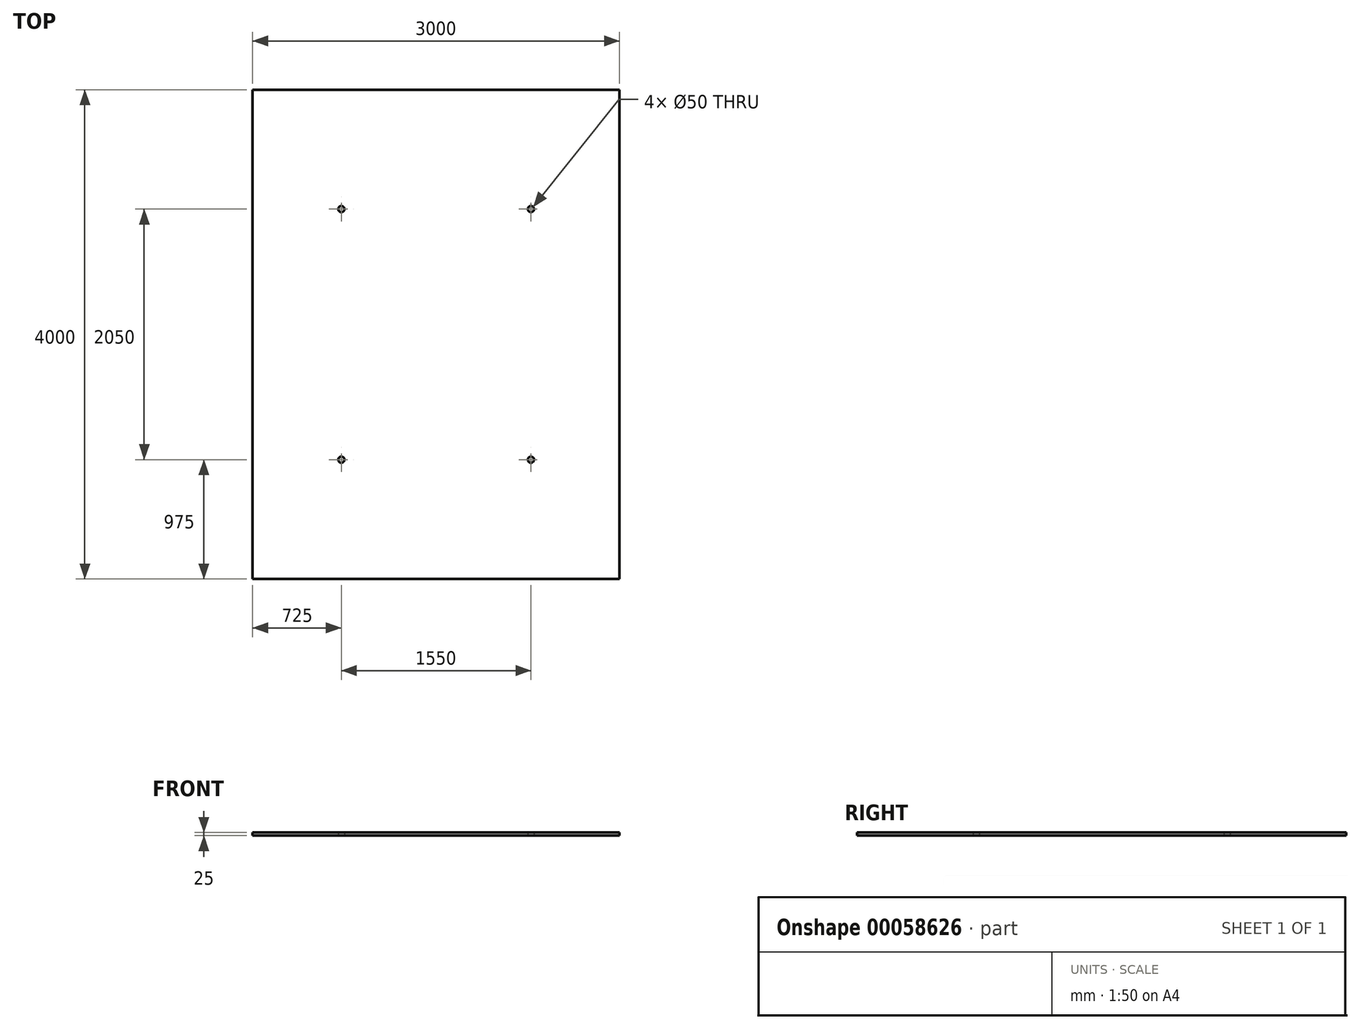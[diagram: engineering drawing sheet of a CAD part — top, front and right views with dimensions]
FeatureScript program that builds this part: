
annotation { "Feature Type Name" : "Feature", "Feature Type Description" : "" }
export const myFeature = defineFeature(function(context is Context, id is Id, definition is map)
    precondition{}
    {
        {
            var Q0;
            Q0=qCreatedBy(makeId("Top.planeOp"),FACE);
            var sketch = newSketch(context, id + "F0", { "sketchPlane" : qUnion([Q0])});
            skLineSegment(sketch, "E0.bottom", {"start": v(0, 0) * mm, "end": v(3000, 0) * mm});
            skLineSegment(sketch, "E0.top", {"start": v(0, 4000) * mm, "end": v(3000, 4000) * mm});
            skLineSegment(sketch, "E0.left", {"start": v(0, 0) * mm, "end": v(0, 4000) * mm});
            skLineSegment(sketch, "E0.right", {"start": v(3000, 0) * mm, "end": v(3000, 4000) * mm});
            skPoint(sketch, "E1.endSnap0", {"position": v(1500, 4000) * mm});
            skLineSegment(sketch, "E2", {"start": v(1500, 0) * mm, "end": v(1500, 4000) * mm, "construction": true});
            skLineSegment(sketch, "E3", {"start": v(0, 2000) * mm, "end": v(3000, 2000) * mm, "construction": true});
            skCircle(sketch, "E4", {"center": v(725, 975) * mm, "radius": 25 * mm});
            skCircle(sketch, "E5", {"center": v(2275, 975) * mm, "radius": 25 * mm});
            skCircle(sketch, "E6", {"center": v(2275, 3025) * mm, "radius": 25 * mm});
            skCircle(sketch, "E7", {"center": v(725, 3025) * mm, "radius": 25 * mm});
            skSolve(sketch);
        }
        {
            var Q0;
            Q0=makeQuery(id+"F0.imprint","IMPRINT",FACE,{"disambiguationData":[TD([[makeQuery(id+"F0.imprint","IMPRINT",EDGE,{"derivedFrom":sQuery(id+"F0.wireOp",EDGE,"E0.bottom")}),1.0]])]});
            extrude(context, id + "F1", {"entities" : qUnion([Q0]), "depth" : 25 * mm});
        }
    });
